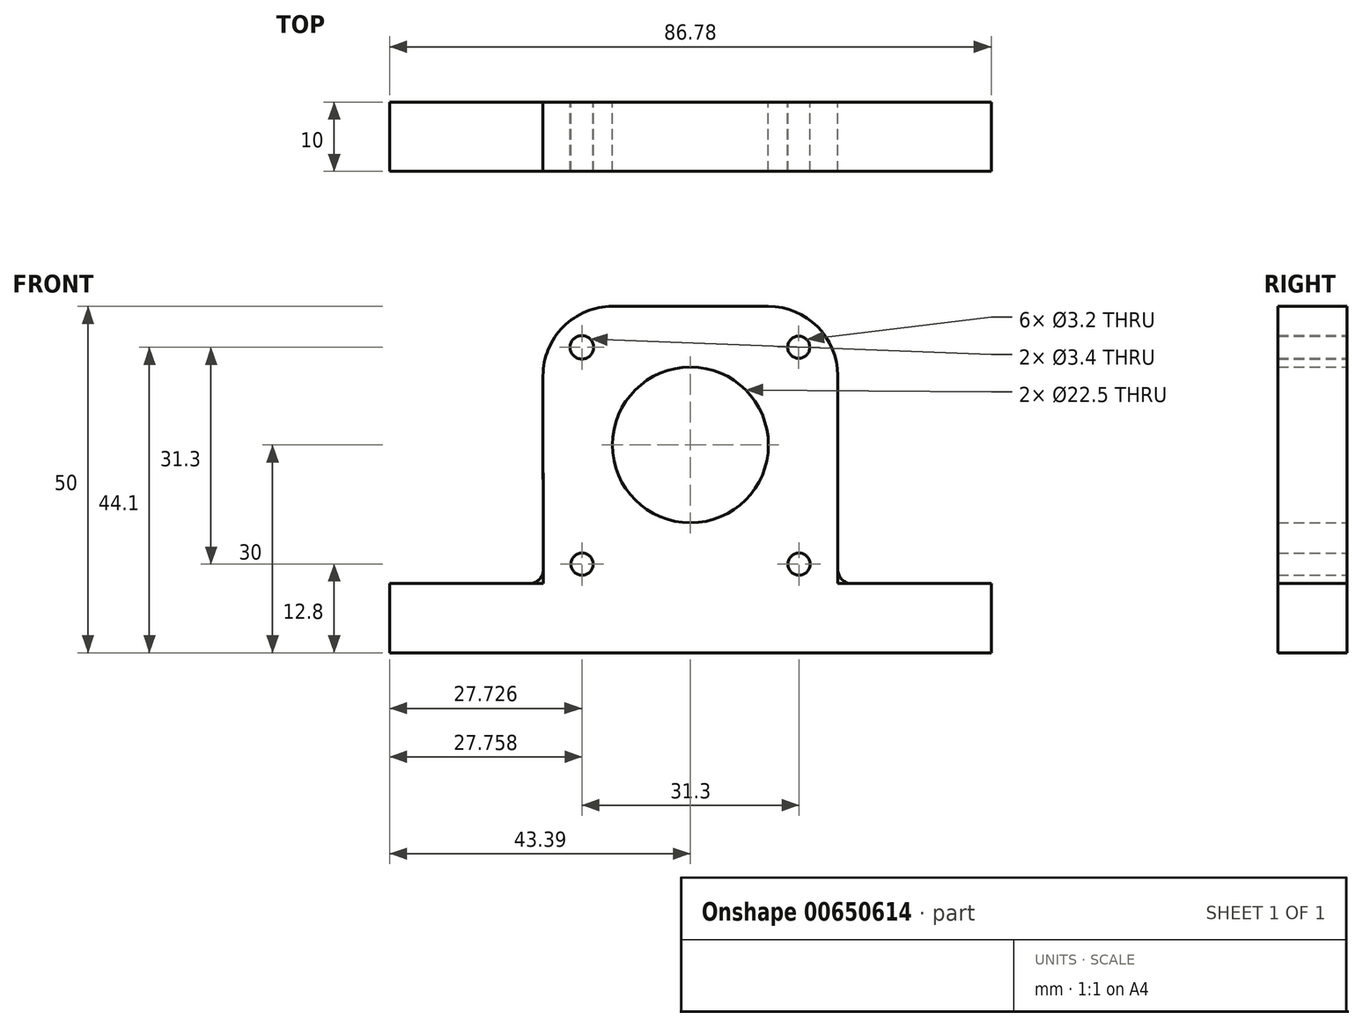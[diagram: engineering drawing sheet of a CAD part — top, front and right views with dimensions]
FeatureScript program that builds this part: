
annotation { "Feature Type Name" : "Feature", "Feature Type Description" : "" }
export const myFeature = defineFeature(function(context is Context, id is Id, definition is map)
    precondition{}
    {
        {
            var Q0;
            Q0=qCreatedBy(makeId("Front.planeOp"),FACE);
            var sketch = newSketch(context, id + "F0", { "sketchPlane" : qUnion([Q0])});
            skLineSegment(sketch, "E0.bottom", {"start": v(-11.26, 20) * mm, "end": v(11.24, 20) * mm});
            skLineSegment(sketch, "E0.left", {"start": v(-21.26, 9.99) * mm, "end": v(-21.23, -20) * mm});
            skLineSegment(sketch, "E0.right", {"start": v(21.24, 10.01) * mm, "end": v(21.27, -20) * mm});
            skPoint(sketch, "E0.middle", {"position": v(0, 0) * mm});
            skPoint(sketch, "E1.orphan", {"position": v(-43.4, -20) * mm});
            skCircle(sketch, "E2", {"center": v(0, 0) * mm, "radius": 11.25 * mm});
            skCircle(sketch, "E3", {"center": v(15.63, 14.1) * mm, "radius": 1.6 * mm});
            skLineSegment(sketch, "E4", {"start": v(21.23, 20) * mm, "end": v(15.63, 20) * mm, "construction": true});
            skLineSegment(sketch, "E5", {"start": v(15.63, 20) * mm, "end": v(15.63, 14.1) * mm, "construction": true});
            skLineSegment(sketch, "E6", {"start": v(21.23, 14.1) * mm, "end": v(15.63, 14.1) * mm, "construction": true});
            skCircle(sketch, "E7", {"center": v(-15.66, 14.1) * mm, "radius": 1.7 * mm});
            skLineSegment(sketch, "E8", {"start": v(-15.66, 14.1) * mm, "end": v(-15.66, 20) * mm, "construction": true});
            skLineSegment(sketch, "E9", {"start": v(-15.66, 14.1) * mm, "end": v(-21.26, 14.1) * mm, "construction": true});
            skCircle(sketch, "E10", {"center": v(15.67, -17.2) * mm, "radius": 1.6 * mm});
            skLineSegment(sketch, "E11", {"start": v(15.67, -17.2) * mm, "end": v(21.27, -17.2) * mm, "construction": true});
            skCircle(sketch, "E12", {"center": v(-15.63, -17.2) * mm, "radius": 1.6 * mm});
            skLineSegment(sketch, "E13", {"start": v(-15.63, -17.2) * mm, "end": v(-21.23, -17.2) * mm, "construction": true});
            skLineSegment(sketch, "E14.bottom", {"start": v(-43.4, -20) * mm, "end": v(-21.23, -20) * mm});
            skLineSegment(sketch, "E14.top", {"start": v(-43.4, -30) * mm, "end": v(43.4, -30) * mm});
            skLineSegment(sketch, "E14.left", {"start": v(-43.4, -20) * mm, "end": v(-43.4, -30) * mm});
            skLineSegment(sketch, "E14.right", {"start": v(43.4, -20) * mm, "end": v(43.4, -30) * mm});
            skPoint(sketch, "E14.middle", {"position": v(0, -25) * mm});
            skLineSegment(sketch, "E15.trimOffspring", {"start": v(21.27, -20) * mm, "end": v(43.4, -20) * mm});
            skLineSegment(sketch, "E16", {"start": v(-15.63, -17.2) * mm, "end": v(-15.63, -30) * mm, "construction": true});
            skLineSegment(sketch, "E17", {"start": v(15.67, -17.2) * mm, "end": v(15.68, -30) * mm, "construction": true});
            skPoint(sketch, "E18.visualSharp", {"position": v(-21.27, 20) * mm});
            skArc(sketch, "E18.filletArc", {"start": v(-11.26, 20) * mm, "mid": v(-18.34, 17.07) * mm, "end": v(-21.26, 9.99) * mm});
            skPoint(sketch, "E19.visualSharp", {"position": v(21.23, 20) * mm});
            skArc(sketch, "E19.filletArc", {"start": v(21.24, 10.01) * mm, "mid": v(18.3, 17.07) * mm, "end": v(11.24, 20) * mm});
            skSolve(sketch);
        }
        {
            var Q0;
            Q0 = qSketchRegion(id + "F0", true);
            extrude(context, id + "F1", {"entities" : qUnion([Q0]), "depth" : 10 * mm, "offsetDistance" : 25 * mm});
        }
        {
            var Q0;
            Q0=makeQuery(id+"F1.opExtrude","SWEPT_EDGE",EDGE,{"disambiguationData":[OSD([sQuery(id+"F0.wireOp",EDGE,"E0.bottom"),sQuery(id+"F0.wireOp",EDGE,"E0.left")])]});
            var Q1;
            Q1=makeQuery(id+"F1.opExtrude","SWEPT_EDGE",EDGE,{"disambiguationData":[OSD([sQuery(id+"F0.wireOp",EDGE,"E0.bottom"),sQuery(id+"F0.wireOp",EDGE,"E0.right")])]});
            fillet(context, id + "F2", {"entities" : qUnion([Q0, Q1]), "radius" : 2 * mm, "tangentPropagation" : true, "allowEdgeOverflow" : false});
        }
        {
            var Q0;
            Q0=makeQuery(id+"F0.imprint","IMPRINT",FACE,{"disambiguationData":[TD([[makeQuery(id+"F0.imprint","IMPRINT",EDGE,{"derivedFrom":sQuery(id+"F0.wireOp",EDGE,"E0.bottom")}),-1.0]])]});
            var Q1;
            Q1=makeQuery(id+"F0.imprint","IMPRINT",FACE,{"disambiguationData":[TD([[makeQuery(id+"F0.imprint","IMPRINT",EDGE,{"derivedFrom":sQuery(id+"F0.wireOp",EDGE,"b5NTWnLL-ywnp-dfcT-Qkwp-JBsaLEyr1V8K.top")}),1.0]])]});
            extrude(context, id + "F3", {"entities" : qUnion([Q0, Q1]), "depth" : 10 * mm, "offsetDistance" : 25 * mm});
        }
    });
